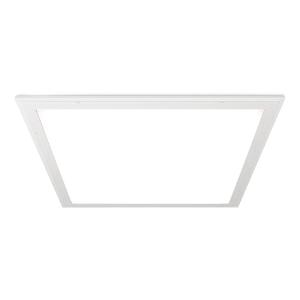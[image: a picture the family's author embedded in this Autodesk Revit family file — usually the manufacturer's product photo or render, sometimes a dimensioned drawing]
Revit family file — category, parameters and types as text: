
# Revit family: 3f_filippi_-_l_650_luce_diffusa_lgs_3f_filippi_-_21868_-_l_650_35w-940_dali_lgs_596x596
name_source: partatom
category: Lighting Fixtures
units: mm (PartAtom-declared; Revit-internal decimal feet)

## family parameters
Cut with Voids When Loaded = No
Host = Face
Light Source = No
Part Type = Normal
Room Calculation Point = No
Round Connector Dimension = Use Diameter
Shared = No

## types (1)
- 3F Filippi - L 650 Luce Diffusa LGS (1 x LED, 3780 lm, 40 W, 4000 K)
    Apparent Load = 40 VA
    Approval mark = ENEC
    CIE Flux Codes = 66 93 98 100 100
    Color Rendering = 90
    Color Temperature = 4000 K
    Control Gear = Electronic transformer
    Default Elevation = 1800 mm
    Description = ILLUMINOTECHNICAL
Luminous efficiency 100% (DLOR 100%, ULOR 0%).
Initial luminous flux of the luminaire 3780 lm.
Direct symmetric distribution.
Installation Interdistance Transv.D = 1.14 x hu - Long.D = 1.16 x hu.
Average luminance <1500 cd/m² for radial angles >65°.
Tabular UGR (CIE 117 - 4H-8H; S=0.25H; 70/50/20): RUG 16.8 - 16.7.
Beam angle: 85° - 85°.
Luminous efficacy 95 lm/W.
Lifetime (L93/B10): 30000 h. (tq+25°C)
Lifetime (L90/B10): 50000 h. (tq+25°C)
Lifetime (L85/B10): 80000 h. (tq+25°C)
Lifetime (L80/B10): 100000 h. (tq+25°C)
Sudden decreased luminous flux after 50000 hours: 0% (C0).
Photobiological safety in compliance with IEC/TR 62778: RG0 risk exempt, (IEC 62471).
In compliance with IEC/EN 62722-2-1 - IEC/EN 62717 standards.

SOURCE
Squared LED module 35W/940.
Source with special protection against aggressive chemically-volatile substances for standard LED technology.
Energy efficiency class (UE 2019/2020 - UE 2019/2015): E.
CIE 13.3 Colour rendering index: CRI >90 (R9 >50%).
IES TM-30 Fidelity Index: Rf = 92 Rg = 101.
CCT nominal colour temperature 4000 K.
Colour initial tolerance (MacAdam): SDCM 3.

MECHANICAL
Housing in galvannealed steel, painted in white epoxy-polyester.
Perimetral frame in white stainless steel.
LGS micro-prismatic flat diffuser in transparent methacrylate (PMMA), multi-lenticular exterior, anti-glare.
Anti-glare opal polycarbonate filter for brightness uniformity.
Luminaire with limited surface temperature. - D - (EN 60598-2-24)
Dimensions: 596x596 mm, height 90 mm. Weight 7 kg.
IP66 protection degree for exposed part, IP64 for recessed part.
Mechanical strength to impacts IK06 (1 joule).
Glow-wire test resistance 650°C.

ELECTRICAL
Halogen Free DALI-2 DATI (Parts 251, 252, 253), PUSH-DIM, electronic wiring 230V-50/60Hz, power factor 0.95 at full load, THD <25%, constant output current, SELV, class I, 1 driver, 1 DALI addresse.
Power of the luminaire 40 W.
CE - IEC 60598-1 - EN 60598-1.
SAFE FLICKER: PstLM=<1 and SVM=<0.4 (IEC TR 61547-1 and IEC TR 63158), to ensure a more comfortable and safe light.
Luminaire compliant with EN 60598-2-22 for power supply from a centralised emergency system CPSS (Central Power Supply System), not incorporated in the luminaire - high risk areas excluded. The default power and flux are 100% in AC and 15% in DC.
Ambient temperature from 0°C to +40°C.
Temperature class T6 max 85°C.
5-pole terminal block (L-N-PE-DA/DA) quick connection for line connection with connection capacity 2x2.5 mm² per poles.
Relative humidity UR: <85%.

INSTALLATION
Lay-in recessed fitting.
All accessories dedicated to this product are available on the Catalog and on our website www.3F-Filippi.com.

APPLICATIONS
Suitable product for food production plants (HACCP), IFS (Food Version 6), BRC (GSFS Food Version 7).
Environments: hospital premises, transit areas, laboratories, platform-roof, underpasses.
Environments: sterilized, aseptic.
In hospital environments, food industry or machines with parts in motion, with considerable sudden temperature changes, and in general in any environments requiring total protection against falling fragments, use luminaires with laminated glass only.
Tempered glass is not immune to falling fragments from harmless and caused by shocks or exceptionally derived from the tempering process.
Environments requiring a high level of protection and simplified cleaning.
Environments with exacting visual tasks, where diffused soft light for optimum visual comfort is required.

LIGHT MANAGEMENT
Recommended minimum setting: 10%.
The luminaire, equipped with (DALI-2 DATI) driver, can be controlled manually with 3F Easy Dim technology or automatically/manually with wired or wireless DALI/D2D control systems.
The D2D driver guarantees interoperability with other devices with the same certification by making the following information available:
Device Data (Part 251), Energy Report (Part 252), Diagnosis & Maintenance (Part 253).
In electrical systems without a regulation system (manual or automatic) and DALI bus, a suitable jumper must be made on the DA-DA terminals of the appliance.

WARNING
Luminaire designed for disposal/recycling at end-of-life.
Replaceable (LED only) light source by a professional. Replaceable control gear by a professional.
    Height = 0 mm  [stored 0 ft]
    Lamp = 1 x LED
    Lamp Light Flux = 3780 lm
    Lamp Power = 40 W
    Lamp count = 1
    Length = 596 mm
    Lifetime = 50000 h
    Luminous efficacy = 95 lm/W
    Manufacturer = 3F Filippi
    ModVariant = No
    Model = 3F Filippi - 21868 - L 650 35W-940 DALI LGS 596x596
    Mounting Place = Ceiling
    Mounting Type = Recessed
    Number of Poles = 1
    OnlyDefault = Yes
    Power Factor = 1
    Product Name = 3F Filippi - L 650 Luce Diffusa LGS
    Product group = recessed luminaire
    ProductGroupID = 4
    Protection Class = Protection class I
    Protection Degree = IP 64
    RLX_Detail_Level = 1
    RLX_Emergency_Light_Flux = 0 lm
    RLX_Emergency_Type = 0
    RLX_Emergency_Type_DB = No
    RlxData = <blob elided: 101013 chars, md5=01b5f87e>
    Socket = socket
    Standby Power = 0 W
    System Light Flux = 3780 lm
    System Power = 40 W
    Type Comments = Product without accessories
    Type Image = 3ffilippi_l_650_luce_diffusa_lgs.jpg
    URL = http://relux.com
    VarID = ---
    Voltage = 0 V
    Weight = 0.00 kg
    Width = 596 mm

note: [stored X ft] marks values corroborated as IEEE doubles in the binary element streams (Revit-internal decimal feet)

## geometry (parser evidence)
native form markers: Blend x4, Sweep x10
no freeform markers — native parametric forms only
